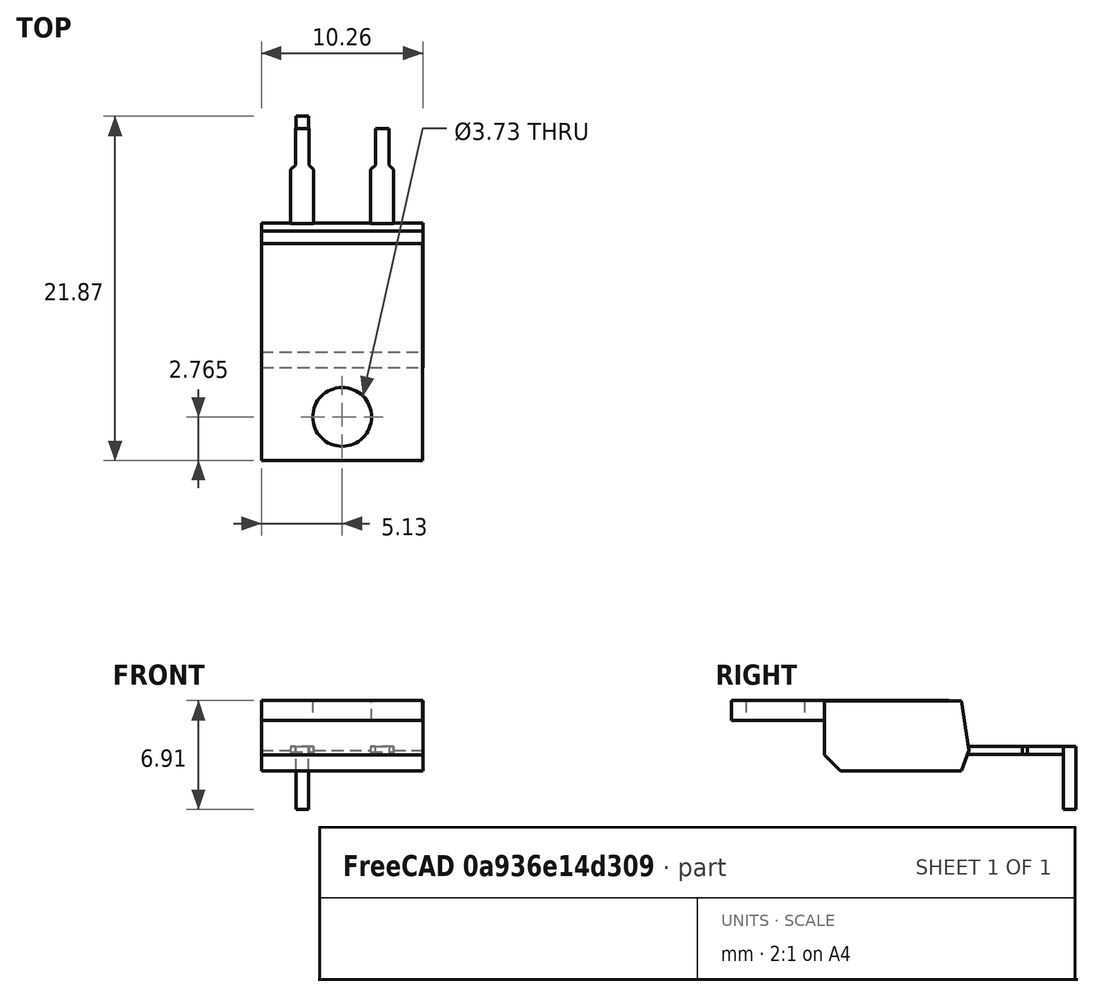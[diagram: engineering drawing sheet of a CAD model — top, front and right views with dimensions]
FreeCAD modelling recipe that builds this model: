
FCSTD DOCUMENT  (FreeCAD 0.20R29177 (Git))
Label: bendedTO220
License: All rights reserved
LicenseURL: http://en.wikipedia.org/wiki/All_rights_reserved
objects: Part::Box×2, Part::Feature×1, Part::Cut×1, Part::Fuse×1, App::Part×1
note: 5 computed .brp shape members not serialized (recipe doc carries the construction recipe); baked Part::Feature solids carry a one-line shape summary decoded from their .brp

FEATURE [Part::Feature] Part__Feature  label="TO-220-2_Vertical"
  Placement = pos=(0,-2.3,3.2) rot=(-1,0,0;4.71239rad)
  shape: bbox 10.25 x 28.53 x 4.455 mm, 37 faces (baked)
FEATURE [Part::Box] Box  label="Cube"
  AttacherType = Attacher::AttachEngine3D
  Height = 10
  Length = 10
  Placement = pos=(-2.8,0,0) rot=(0,0,1;0rad)
  Width = 10
FEATURE [Part::Cut] Cut
  Base = -> Part__Feature
  Tool = -> Box
FEATURE [Part::Box] Box001  label="Cube001"
  AttacherType = Attacher::AttachEngine3D
  Height = 4
  Length = 0.8
  Placement = pos=(-0.4,0,-0.55) rot=(0,0,1;0rad)
  Width = 0.8
FEATURE [Part::Fuse] Fusion
  Base = -> Cut
  Tool = -> Box001
FEATURE [App::Part] Part
  Group = -> [Part__Feature,Box,Cut,Box001,Fusion]
  Origin = -> Origin
